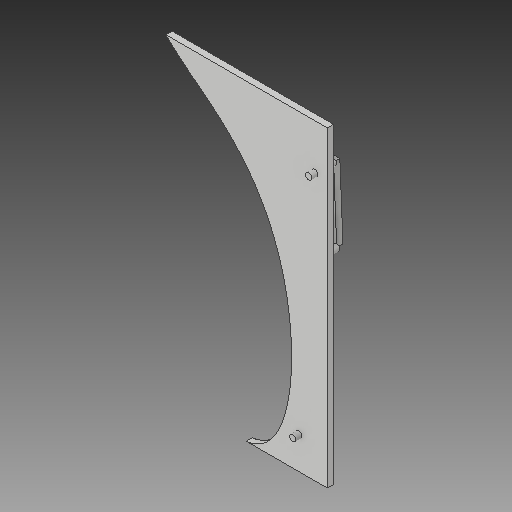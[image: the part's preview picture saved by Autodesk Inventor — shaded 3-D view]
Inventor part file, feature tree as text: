
AUTODESK INVENTOR PART (.ipt)
format: ipt  version: 2018 (Build 220112000, 112)  size: 153,600 bytes
history: native  units: in
note: dims shown in document units (in); Inventor stores cm internally (conversion verified against a paired STEP export)
features: sketch x6, other x3
ambient origin geometry x8: Origin, YZ Plane, XZ Plane, XY Plane, X Axis, Y Axis, Z Axis, Center Point
bodies: Solid1 (feature_tree)
feature tree (9):
  other  "side frame"
  other  "Solid1::side frame"
  other  "TaggingFeature1"
  sketch  "Sketch1"  dims[d0=0.3937in]
  sketch  "Sketch2"
  sketch  "Sketch3"
  sketch  "Sketch4"
  sketch  "Sketch6"
  sketch  "Sketch8"
